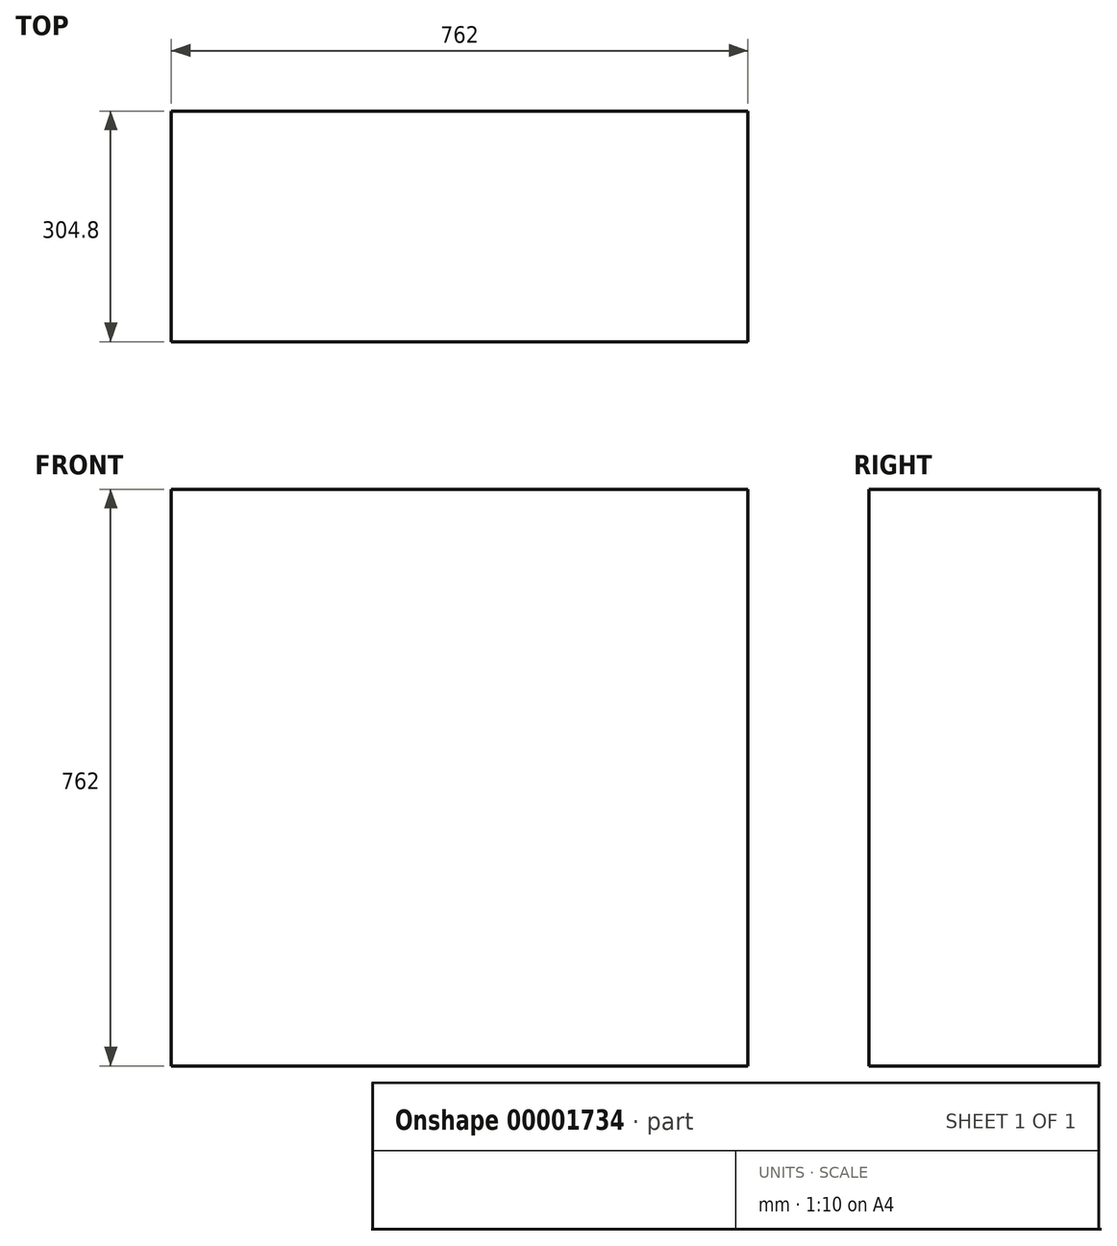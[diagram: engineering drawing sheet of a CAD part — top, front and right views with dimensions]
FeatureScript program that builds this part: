
annotation { "Feature Type Name" : "Feature", "Feature Type Description" : "" }
export const myFeature = defineFeature(function(context is Context, id is Id, definition is map)
    precondition{}
    {
        {
            var Q0;
            Q0=qCreatedBy(makeId("Front.planeOp"),FACE);
            var sketch = newSketch(context, id + "F0", { "sketchPlane" : qUnion([Q0])});
            skLineSegment(sketch, "E0.bottom", {"start": v(381, 381) * mm, "end": v(-381, 381) * mm});
            skLineSegment(sketch, "E0.top", {"start": v(381, -381) * mm, "end": v(-381, -381) * mm});
            skLineSegment(sketch, "E0.left", {"start": v(381, 381) * mm, "end": v(381, -381) * mm});
            skLineSegment(sketch, "E0.right", {"start": v(-381, 381) * mm, "end": v(-381, -381) * mm});
            skPoint(sketch, "E0.middle", {"position": v(0, 0) * mm});
            skSolve(sketch);
        }
        {
            var Q0;
            Q0=makeQuery(id+"F0.imprint","IMPRINT",FACE,{"disambiguationData":[TD([[makeQuery(id+"F0.imprint","IMPRINT",EDGE,{"derivedFrom":sQuery(id+"F0.wireOp",EDGE,"E0.bottom")}),1.0]])]});
            extrude(context, id + "F1", {"entities" : qUnion([Q0]), "endBound" : BoundingType.SYMMETRIC, "depth" : 304.8 * mm, "offsetDistance" : 25.4 * mm});
        }
    });
